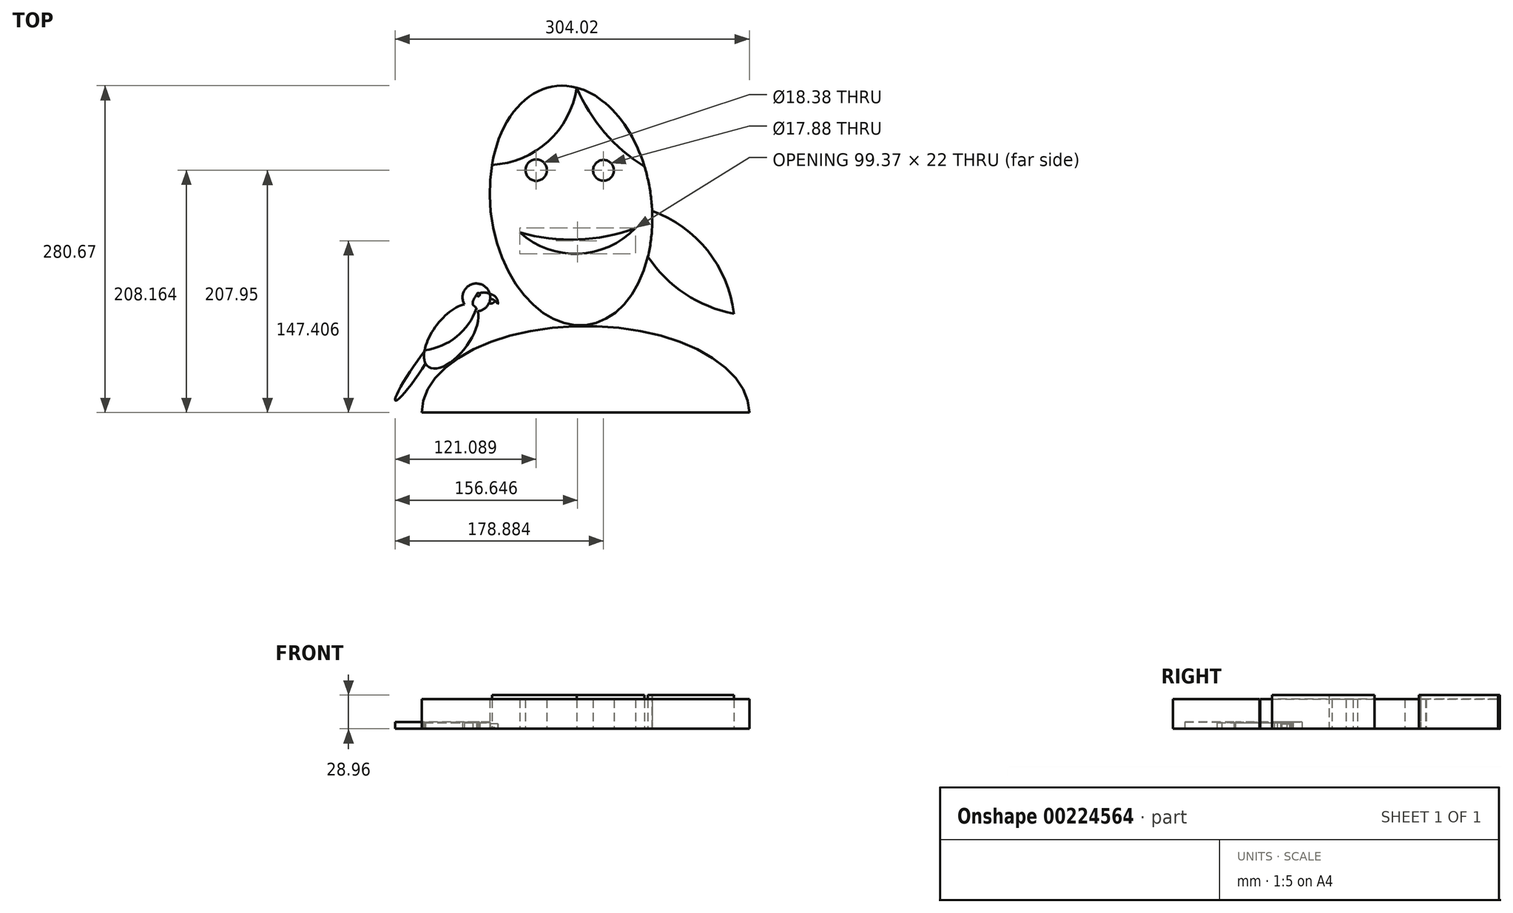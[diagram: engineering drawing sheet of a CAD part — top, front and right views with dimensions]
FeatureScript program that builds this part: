
annotation { "Feature Type Name" : "Feature", "Feature Type Description" : "" }
export const myFeature = defineFeature(function(context is Context, id is Id, definition is map)
    precondition{}
    {
        {
            var Q0;
            Q0=qCreatedBy(makeId("Top.planeOp"),FACE);
            var sketch = newSketch(context, id + "F0", { "sketchPlane" : qUnion([Q0])});
            skCircle(sketch, "E0", {"center": v(-29.86, 30.4) * mm, "radius": 9.2 * mm});
            skCircle(sketch, "E1", {"center": v(27.93, 30.18) * mm, "radius": 8.94 * mm});
            skArc(sketch, "E2", {"start": v(-43.99, -23.12) * mm, "mid": v(6.46, -41.36) * mm, "end": v(55.38, -19.36) * mm});
            skArc(sketch, "E3", {"start": v(-43.99, -23.12) * mm, "mid": v(6, -29.22) * mm, "end": v(55.38, -19.36) * mm});
            skEllipse(sketch, "E4", {"center": v(0, 0) * mm, "majorRadius": 103.41 * mm, "minorRadius": 69.02 * mm, "majorAxis": v(-0.13, 1)});
            skArc(sketch, "E5", {"start": v(-67.86, 34.9) * mm, "mid": v(-19.6, 55.03) * mm, "end": v(4.9, 101.22) * mm});
            skArc(sketch, "E6", {"start": v(4.9, 101.22) * mm, "mid": v(28.74, 62.82) * mm, "end": v(63.1, 33.47) * mm});
            skArc(sketch, "E7", {"start": v(139.72, -92.72) * mm, "mid": v(110.14, -30.66) * mm, "end": v(48.87, 0.53) * mm});
            skArc(sketch, "E8", {"start": v(48.87, 0.53) * mm, "mid": v(79.44, -60.57) * mm, "end": v(139.72, -92.72) * mm});
            skEllipticalArc(sketch, "E9", {});
            skLineSegment(sketch, "E10", {"start": v(-128.13, -177.77) * mm, "end": v(153.07, -177.77) * mm});
            skEllipse(sketch, "E11", {"center": v(-102.85, -112.21) * mm, "majorRadius": 32.73 * mm, "minorRadius": 15.64 * mm, "majorAxis": v(0.6, 0.8)});
            skArc(sketch, "E12", {"start": v(-125.66, -124.15) * mm, "mid": v(-98.24, -112.6) * mm, "end": v(-81.18, -88.24) * mm});
            skEllipticalArc(sketch, "E13", {});
            skArc(sketch, "E14", {"start": v(-80.08, -90.71) * mm, "mid": v(-75.75, -68.27) * mm, "end": v(-91.54, -84.8) * mm});
            skArc(sketch, "E15", {"start": v(-62.86, -84.6) * mm, "mid": v(-64.37, -78.81) * mm, "end": v(-69.65, -76) * mm});
            skArc(sketch, "E16", {"start": v(-62.86, -84.6) * mm, "mid": v(-65.57, -81.54) * mm, "end": v(-69.35, -79.98) * mm});
            skArc(sketch, "E17", {"start": v(-70.4, -83.83) * mm, "mid": v(-67.4, -83.88) * mm, "end": v(-65.29, -81.75) * mm});
            skCircle(sketch, "E18", {"center": v(-79.6, -76.48) * mm, "radius": 1.35 * mm});
            skArc(sketch, "E19", {"start": v(-69.65, -76) * mm, "mid": v(-74.1, -74.63) * mm, "end": v(-78.67, -75.5) * mm});
            skArc(sketch, "E20.trimOffspring", {"start": v(-80.88, -76.9) * mm, "mid": v(-83.63, -80.73) * mm, "end": v(-84.26, -85.4) * mm});
            const initialGuessF0  = {"E9": [0.012469829991459846, -0.17777232825756073, 0, 1, 0.07437434047460556, 0.14059640235877505, 4.71238898038469, 1.5707963267948966], "E13": [-0.13258621096611029, -0.14084605127573013, 0.5631095930772618, 0.826382227655194, 0.03214720585017629, 0.0037044352588746945, 1.0292882328374924, 4.983947689362255]};
            skSetInitialGuess(sketch, initialGuessF0);
            skSolve(sketch);
        }
        {
            var Q0;
            Q0=makeQuery(id+"F0.imprint","IMPRINT",FACE,{"disambiguationData":[TD([[makeQuery(id+"F0.imprint","IMPRINT",EDGE,{"derivedFrom":sQuery(id+"F0.wireOp",EDGE,"E0")}),-1.0]])]});
            var Q1;
            {var subQ6=sQuery(id+"F0.wireOp",EDGE,"E3");var subQ7=sQuery(id+"F0.wireOp",EDGE,"E2");var subQ8=makeQuery(id+"F0.imprint","INTERSECT",VERTEX,{"disambiguationData":[OD(1.0)],"derivedFrom":[subQ7,subQ6]});Q1=makeQuery(id+"F0.imprint","IMPRINT",FACE,{"disambiguationData":[TD([[makeQuery(id+"F0.imprint","IMPRINT",EDGE,{"disambiguationData":[TD([[subQ8,1.0]])],"derivedFrom":subQ7}),-1.0]])]});}
            extrude(context, id + "F1", {"entities" : qUnion([Q0, Q1]), "depth" : 25.4 * mm});
        }
        {
            var Q0;
            {var subQ0=sQuery(id+"F0.wireOp",EDGE,"E5");Q0=makeQuery(id+"F0.imprint","IMPRINT",FACE,{"disambiguationData":[TD([[makeQuery(id+"F0.imprint","IMPRINT",EDGE,{"derivedFrom":subQ0}),1.0]])]});}
            var Q1;
            {var subQ0=sQuery(id+"F0.wireOp",EDGE,"E6");Q1=makeQuery(id+"F0.imprint","IMPRINT",FACE,{"disambiguationData":[TD([[makeQuery(id+"F0.imprint","IMPRINT",EDGE,{"derivedFrom":subQ0}),1.0]])]});}
            var Q2;
            {var subQ0=sQuery(id+"F0.wireOp",EDGE,"E8");var subQ1=sQuery(id+"F0.wireOp",EDGE,"E4");var subQ2=makeQuery(id+"F0.imprint","INTERSECT",VERTEX,{"derivedFrom":[subQ1,subQ0]});Q2=makeQuery(id+"F0.imprint","IMPRINT",FACE,{"disambiguationData":[TD([[makeQuery(id+"F0.imprint","IMPRINT",EDGE,{"disambiguationData":[TD([[subQ2,-1.0]])],"derivedFrom":subQ1}),-1.0]])]});}
            extrude(context, id + "F2", {"entities" : qUnion([Q0, Q1, Q2]), "depth" : 28.96 * mm});
        }
        {
            var Q0;
            {var subQ7=sQuery(id+"F0.wireOp",EDGE,"E19");Q0=makeQuery(id+"F0.imprint","IMPRINT",FACE,{"disambiguationData":[TD([[makeQuery(id+"F0.imprint","IMPRINT",EDGE,{"derivedFrom":subQ7}),1.0]])]});}
            var Q1;
            {var subQ0=sQuery(id+"F0.wireOp",EDGE,"E12");Q1=makeQuery(id+"F0.imprint","IMPRINT",FACE,{"disambiguationData":[TD([[makeQuery(id+"F0.imprint","IMPRINT",EDGE,{"derivedFrom":subQ0}),-1.0]])]});}
            extrude(context, id + "F3", {"entities" : qUnion([Q0, Q1]), "depth" : 5.33 * mm});
        }
        {
            var Q0;
            {var subQ0=sQuery(id+"F0.wireOp",EDGE,"E19");Q0=makeQuery(id+"F0.imprint","IMPRINT",FACE,{"disambiguationData":[TD([[makeQuery(id+"F0.imprint","IMPRINT",EDGE,{"derivedFrom":subQ0}),-1.0]])]});}
            var Q1;
            {var subQ3=sQuery(id+"F0.wireOp",EDGE,"E12");Q1=makeQuery(id+"F0.imprint","IMPRINT",FACE,{"disambiguationData":[TD([[makeQuery(id+"F0.imprint","IMPRINT",EDGE,{"derivedFrom":subQ3}),1.0]])]});}
            var Q2;
            {var subQ0=sQuery(id+"F0.wireOp",EDGE,"E13");Q2=makeQuery(id+"F0.imprint","IMPRINT",FACE,{"disambiguationData":[TD([[makeQuery(id+"F0.imprint","IMPRINT",EDGE,{"derivedFrom":subQ0}),1.0]])]});}
            extrude(context, id + "F4", {"entities" : qUnion([Q0, Q1, Q2]), "depth" : 5.84 * mm});
        }
        {
            var Q0;
            {var subQ0=sQuery(id+"F0.wireOp",EDGE,"E18");var subQ1=makeQuery(id+"F0.imprint","INTERSECT",VERTEX,{"derivedFrom":[subQ0,sQuery(id+"F0.wireOp",EDGE,"E19")]});Q0=makeQuery(id+"F0.imprint","IMPRINT",FACE,{"disambiguationData":[TD([[makeQuery(id+"F0.imprint","IMPRINT",EDGE,{"disambiguationData":[TD([[subQ1,-1.0]])],"derivedFrom":subQ0}),1.0]])]});}
            extrude(context, id + "F5", {"entities" : qUnion([Q0]), "depth" : 4.06 * mm});
        }
        {
            var Q0;
            {var subQ0=sQuery(id+"F0.wireOp",EDGE,"E15");Q0=makeQuery(id+"F0.imprint","IMPRINT",FACE,{"disambiguationData":[TD([[makeQuery(id+"F0.imprint","IMPRINT",EDGE,{"derivedFrom":subQ0}),1.0]])]});}
            extrude(context, id + "F6", {"entities" : qUnion([Q0]), "depth" : 4.4 * mm});
        }
        {
            var Q0;
            {var subQ3=sQuery(id+"F0.wireOp",EDGE,"E17");Q0=makeQuery(id+"F0.imprint","IMPRINT",FACE,{"disambiguationData":[TD([[makeQuery(id+"F0.imprint","IMPRINT",EDGE,{"derivedFrom":subQ3}),1.0]])]});}
            extrude(context, id + "F7", {"entities" : qUnion([Q0]), "operationType" : NewBodyOperationType.ADD, "depth" : 1.14 * mm});
        }
        {
            var Q0;
            Q0=makeQuery(id+"F0.imprint","IMPRINT",FACE,{"disambiguationData":[TD([[makeQuery(id+"F0.imprint","IMPRINT",EDGE,{"derivedFrom":sQuery(id+"F0.wireOp",EDGE,"E9")}),1.0]])]});
            extrude(context, id + "F8", {"entities" : qUnion([Q0]), "depth" : 25.4 * mm});
        }
    });
